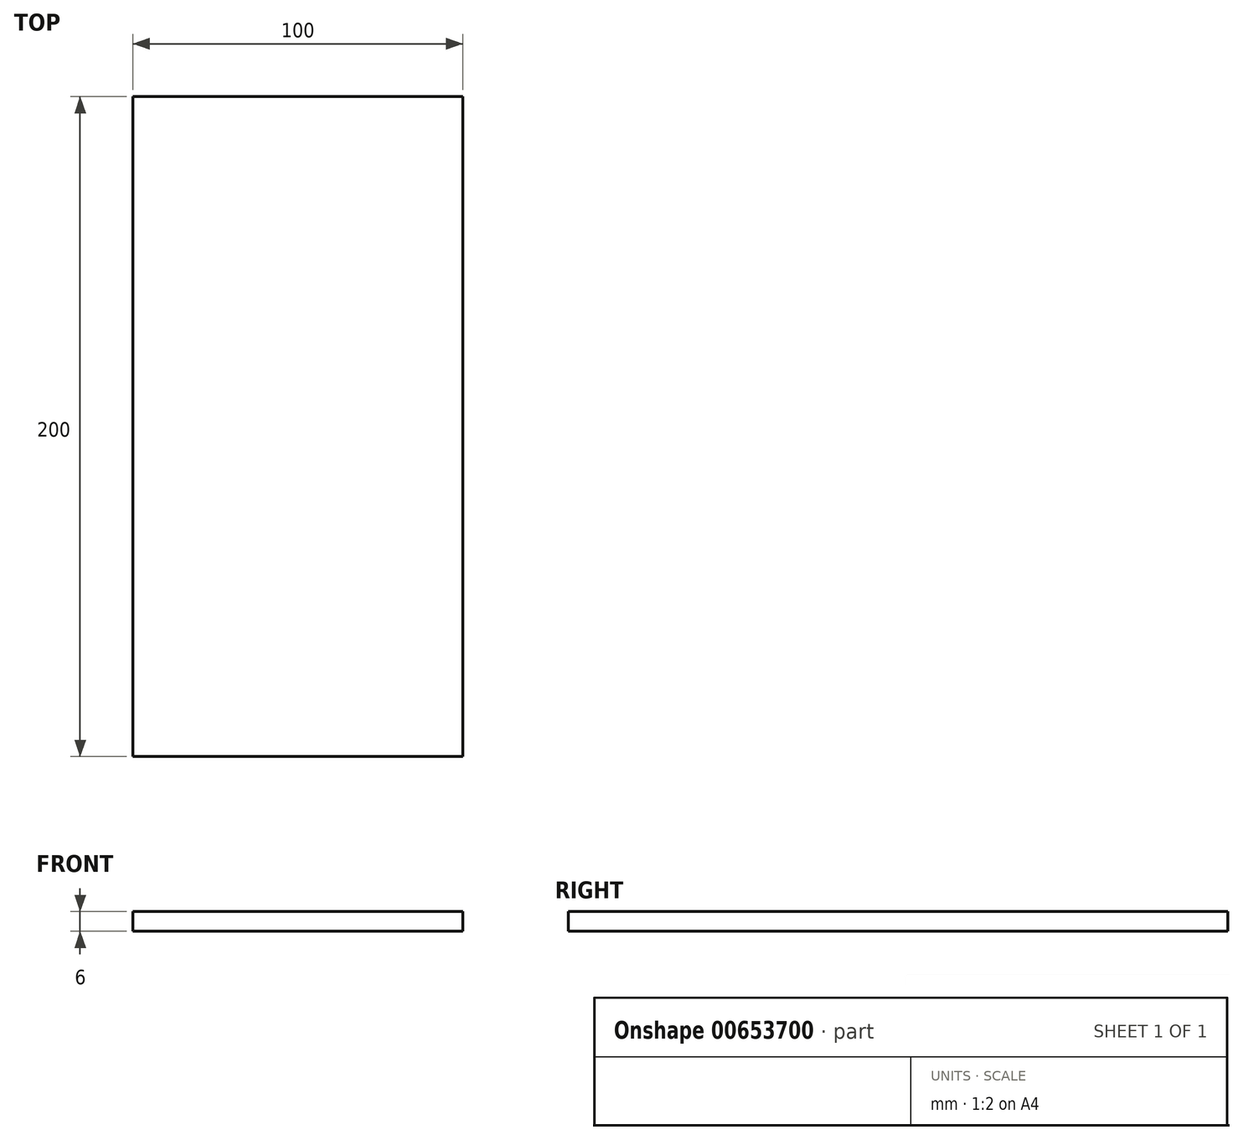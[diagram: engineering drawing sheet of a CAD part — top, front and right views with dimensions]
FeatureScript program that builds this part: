
annotation { "Feature Type Name" : "Feature", "Feature Type Description" : "" }
export const myFeature = defineFeature(function(context is Context, id is Id, definition is map)
    precondition{}
    {
        {
            var Q0;
            Q0=qCreatedBy(makeId("Top.planeOp"),FACE);
            var sketch = newSketch(context, id + "F0", { "sketchPlane" : qUnion([Q0])});
            skLineSegment(sketch, "E0.bottom", {"start": v(0, 99.3) * mm, "end": v(100, 99.3) * mm});
            skLineSegment(sketch, "E0.top", {"start": v(0, -100.7) * mm, "end": v(100, -100.7) * mm});
            skLineSegment(sketch, "E0.left", {"start": v(0, 99.3) * mm, "end": v(0, -100.7) * mm});
            skLineSegment(sketch, "E0.right", {"start": v(100, 99.3) * mm, "end": v(100, -100.7) * mm});
            skSolve(sketch);
        }
        {
            var Q0;
            Q0=makeQuery(id+"F0.imprint","IMPRINT",FACE,{"disambiguationData":[TD([[makeQuery(id+"F0.imprint","IMPRINT",EDGE,{"derivedFrom":sQuery(id+"F0.wireOp",EDGE,"E0.bottom")}),-1.0]])]});
            extrude(context, id + "F1", {"entities" : qUnion([Q0]), "endBound" : BoundingType.SYMMETRIC, "oppositeDirection" : true, "depth" : 6 * mm, "offsetDistance" : 25 * mm});
        }
    });
